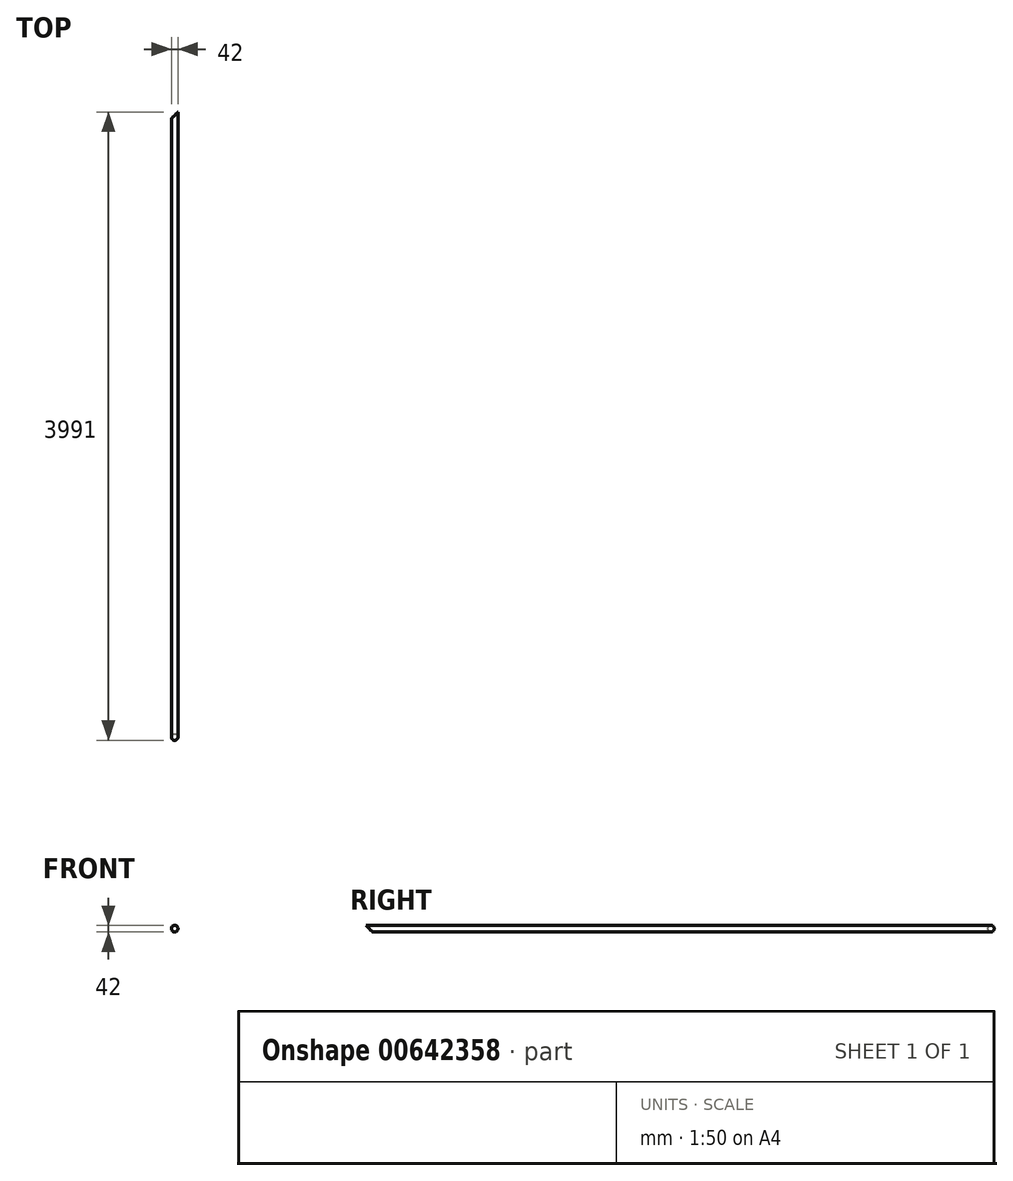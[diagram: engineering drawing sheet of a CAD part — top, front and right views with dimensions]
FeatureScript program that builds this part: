
annotation { "Feature Type Name" : "Feature", "Feature Type Description" : "" }
export const myFeature = defineFeature(function(context is Context, id is Id, definition is map)
    precondition{}
    {
        {
            var Q0;
            Q0=qCreatedBy(makeId("Front.planeOp"),FACE);
            var sketch = newSketch(context, id + "F0", { "sketchPlane" : qUnion([Q0])});
            skLineSegment(sketch, "E0.bottom", {"start": v(21, 21) * mm, "end": v(-21, 21) * mm});
            skLineSegment(sketch, "E0.top", {"start": v(21, -21) * mm, "end": v(-21, -21) * mm});
            skLineSegment(sketch, "E0.left", {"start": v(21, 21) * mm, "end": v(21, -21) * mm});
            skLineSegment(sketch, "E0.right", {"start": v(-21, 21) * mm, "end": v(-21, -21) * mm});
            skPoint(sketch, "E0.middle", {"position": v(0, 0) * mm});
            skSolve(sketch);
        }
        {
            var Q0;
            Q0=makeQuery(id+"F0.imprint","IMPRINT",FACE,{"disambiguationData":[TD([[makeQuery(id+"F0.imprint","IMPRINT",EDGE,{"derivedFrom":sQuery(id+"F0.wireOp",EDGE,"E0.bottom")}),1.0]])]});
            extrude(context, id + "F1", {"entities" : qUnion([Q0]), "depth" : (4020 - 29) * mm, "offsetDistance" : 25 * mm});
        }
        {
            var Q0;
            Q0=makeQuery(id+"F1.opExtrude","SWEPT_FACE",FACE,{"disambiguationData":[OSD([sQuery(id+"F0.wireOp",EDGE,"E0.left")])]});
            var sketch = newSketch(context, id + "F2", { "sketchPlane" : qUnion([Q0])});
            skLineSegment(sketch, "E1", {"start": v(-3991, 21) * mm, "end": v(-3949, -21) * mm});
            skSolve(sketch);
        }
        {
            var Q0;
            {var subQ0=sQuery(id+"F2.wireOp",EDGE,"E1");Q0=makeQuery(id+"F2.imprint","IMPRINT",FACE,{"disambiguationData":[TD([[makeQuery(id+"F2.imprint","IMPRINT",EDGE,{"derivedFrom":subQ0}),-1.0]])]});}
            extrude(context, id + "F3", {"entities" : qUnion([Q0]), "operationType" : NewBodyOperationType.REMOVE, "oppositeDirection" : true, "depth" : 100 * mm, "offsetDistance" : 25 * mm});
        }
        {
            var Q0;
            Q0=makeQuery(id+"F1.opExtrude","SWEPT_FACE",FACE,{"disambiguationData":[OSD([sQuery(id+"F0.wireOp",EDGE,"E0.top")])]});
            var sketch = newSketch(context, id + "F4", { "sketchPlane" : qUnion([Q0])});
            skLineSegment(sketch, "E2", {"start": v(21, 0) * mm, "end": v(-21, 42) * mm});
            skSolve(sketch);
        }
        {
            var Q0;
            {var subQ0=sQuery(id+"F4.wireOp",EDGE,"E2");Q0=makeQuery(id+"F4.imprint","IMPRINT",FACE,{"disambiguationData":[TD([[makeQuery(id+"F4.imprint","IMPRINT",EDGE,{"derivedFrom":subQ0}),1.0]])]});}
            extrude(context, id + "F5", {"entities" : qUnion([Q0]), "operationType" : NewBodyOperationType.REMOVE, "oppositeDirection" : true, "depth" : 100 * mm, "offsetDistance" : 25 * mm});
        }
        {
            var Q0;
            Q0=makeQuery(id+"F1.opExtrude","SWEPT_EDGE",EDGE,{"disambiguationData":[OSD([sQuery(id+"F0.wireOp",EDGE,"E0.top"),sQuery(id+"F0.wireOp",EDGE,"E0.right")])]});
            var Q1;
            Q1=makeQuery(id+"F1.opExtrude","SWEPT_EDGE",EDGE,{"disambiguationData":[OSD([sQuery(id+"F0.wireOp",EDGE,"E0.top"),sQuery(id+"F0.wireOp",EDGE,"E0.left")])]});
            var Q2;
            Q2=makeQuery(id+"F1.opExtrude","SWEPT_EDGE",EDGE,{"disambiguationData":[OSD([sQuery(id+"F0.wireOp",EDGE,"E0.bottom"),sQuery(id+"F0.wireOp",EDGE,"E0.left")])]});
            var Q3;
            Q3=makeQuery(id+"F1.opExtrude","SWEPT_EDGE",EDGE,{"disambiguationData":[OSD([sQuery(id+"F0.wireOp",EDGE,"E0.bottom"),sQuery(id+"F0.wireOp",EDGE,"E0.right")])]});
            fillet(context, id + "F6", {"entities" : qUnion([Q0, Q1, Q2, Q3]), "radius" : 21 * mm, "tangentPropagation" : true, "allowEdgeOverflow" : false});
        }
    });
